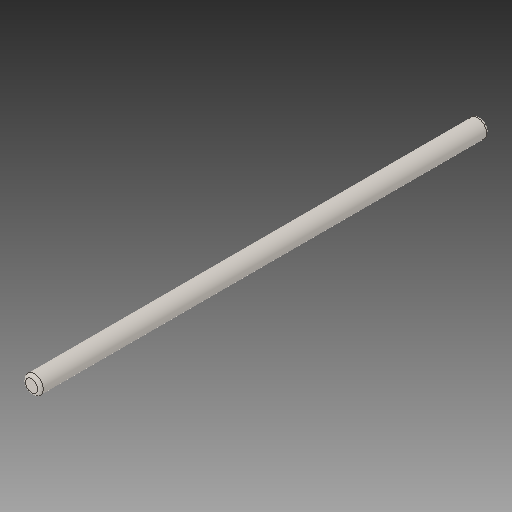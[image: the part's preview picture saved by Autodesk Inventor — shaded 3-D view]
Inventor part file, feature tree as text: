
AUTODESK INVENTOR PART (.ipt)
format: ipt  version: 2019 (Build 230136000, 136)  size: 83,456 bytes
history: native  units: in
note: dims shown in document units (in); Inventor stores cm internally (conversion verified against a paired STEP export)
features: fillet x1
ambient origin geometry x8: Origin, YZ Plane, XZ Plane, XY Plane, X Axis, Y Axis, Z Axis, Center Point
bodies: Solid1 (feature_tree)
feature tree (1):
  fillet  "Fillet1"  [1 undecoded]
note: 1 required parameter value undecoded (feature->parameter linkage not recoverable at this tier; creation-order binding heuristic only, values carry confidence <= 0.55)
